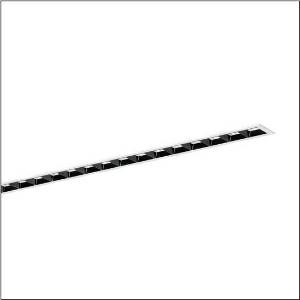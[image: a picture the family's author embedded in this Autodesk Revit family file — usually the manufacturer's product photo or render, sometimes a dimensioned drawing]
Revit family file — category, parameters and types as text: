
# Revit family: silica_r__21_51mx12db45wb_7f54
name_source: partatom
category: Lighting Fixtures
units: mm (PartAtom-declared; Revit-internal decimal feet)

## family parameters
Cut with Voids When Loaded = No
Host = Face
Light Source = No
Part Type = Normal
Room Calculation Point = No
Round Connector Dimension = Use Diameter
Shared = No

## types (1)
- --- (1 x LED, 5400 lm, 32 W, 4000K)
    Apparent Load = 32 VA
    CIE Flux Codes = 86 100 100 100 100
    Color Rendering = 80
    Color Temperature = 4000K
    Default Elevation = 1800 mm
    Description = Silica® 21, office luminaire, primary light control with darklight reflector, of PMMA, black, CAT 2 (L<= 3000cd/m²), light emission: direct distribution, primary light characteristic: symmetric, installation type: recessed, LED, rated luminous flux: 5.400lm, luminous efficacy: 169lm/W, light colour: 840, colour temperature: 4000K, control gear: DALI 2, with terminal, 3+2-pole, max. 2.5mm², mains connection: 220..240V, AC, 50/60Hz, rated input power: 32W, luminaire housing, of aluminium, traffic white (RAL 9016), length: 1.528mm, width: 79mm, height: 53mm, protection rating (complete): IP20, insulation class (complete): insulation class I (protective earthing), certification: CE, ENEC, VDE, permissible operating ambient temperature: 0..+35°C, standard: EN 50419, packaging unit: 1 piece
    Height = 0 mm  [stored 0 ft]
    Lamp = 1 x LED
    Lamp Light Flux = 5400 lm
    Lamp Power = 32 W
    Lamp count = 1
    Length = 1527 mm
    Luminous efficacy = 169 lm/W
    Manufacturer = Siteco
    ModVariant = No
    Model = 51MX12DB45WB
    Mounting Place = Ceiling
    Mounting Type = Recessed
    Number of Poles = 1
    OnlyDefault = Yes
    Power Factor = 1
    Product Name = Silica® 21
    Product group = office luminaire | ceiling recessed
    ProductGroupID = 401
    Protection Class = Protection class I
    Protection Degree = IP 20
    RLX_Detail_Level = 1
    RLX_Emergency_Light_Flux = 0 lm
    RLX_Emergency_Type = 0
    RLX_Emergency_Type_DB = No
    RlxData = <blob elided: 42441 chars, md5=377e4624>
    Socket = socket
    Standby Power = 0 W
    System Light Flux = 5400 lm
    System Power = 32 W
    Type Comments = factory setting: luminous flux: 100 % | dim-lin: 254 | 366 mA
    Type Image = l_1335880.jpg
    URL = http://relux.com
    VarID = @adj_124462
    Voltage = 0 V
    Weight = 0.00 kg
    Width = 79 mm

note: [stored X ft] marks values corroborated as IEEE doubles in the binary element streams (Revit-internal decimal feet)

## geometry (parser evidence)
native form markers: Blend x4, Sweep x10
no freeform markers — native parametric forms only
